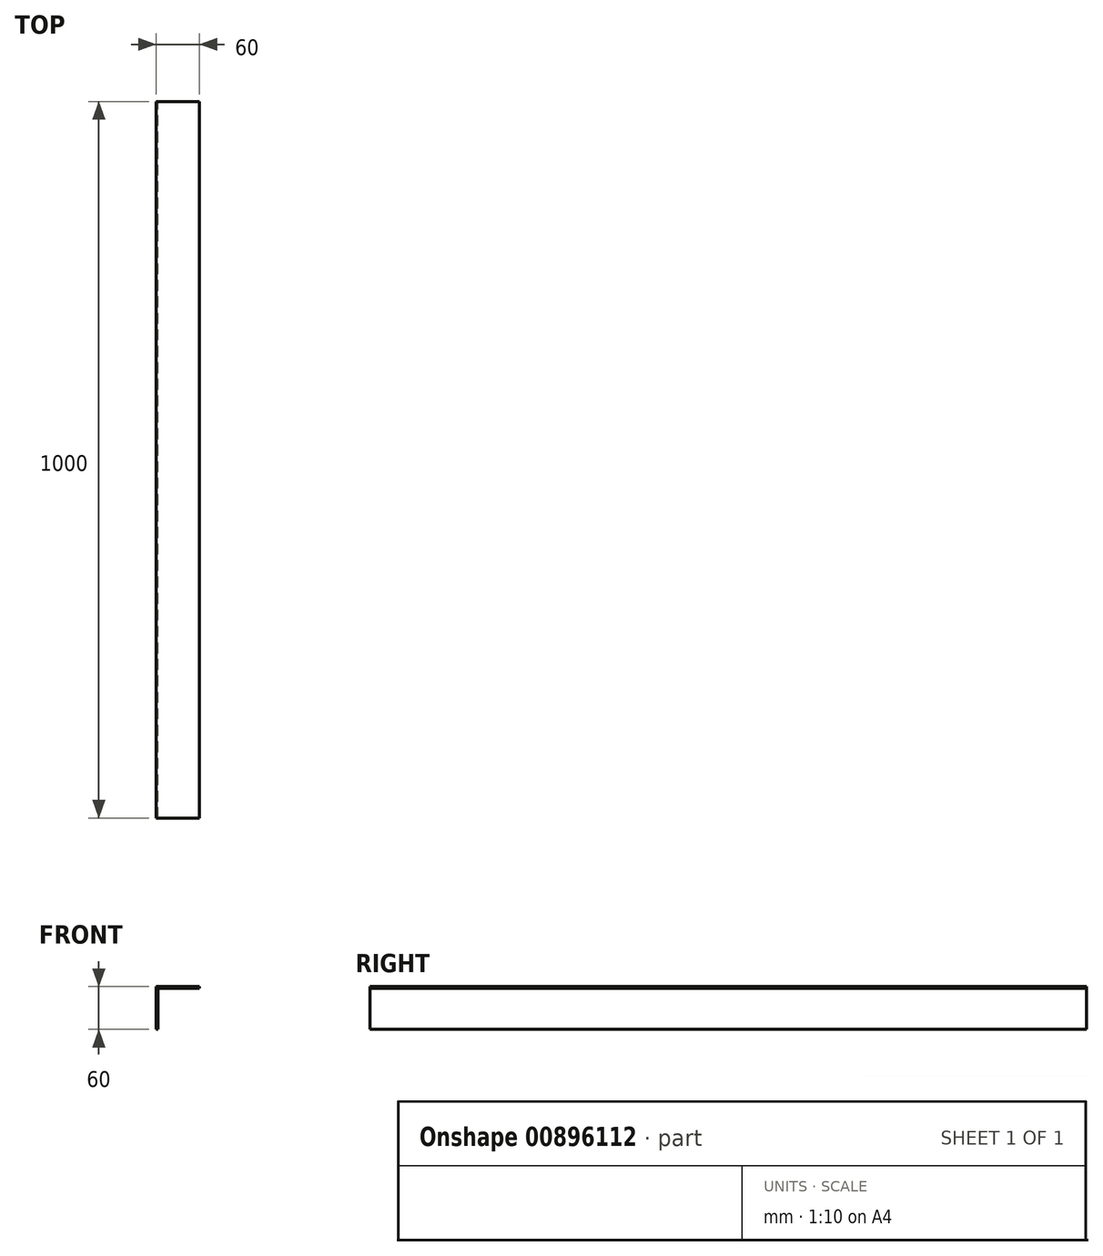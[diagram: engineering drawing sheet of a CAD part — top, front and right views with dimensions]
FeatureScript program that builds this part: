
annotation { "Feature Type Name" : "Feature", "Feature Type Description" : "" }
export const myFeature = defineFeature(function(context is Context, id is Id, definition is map)
    precondition{}
    {
        {
            var Q0;
            Q0=qCreatedBy(makeId("Front.planeOp"),FACE);
            var sketch = newSketch(context, id + "F0", { "sketchPlane" : qUnion([Q0])});
            skLineSegment(sketch, "E0", {"start": v(0, 0) * mm, "end": v(60, 0) * mm});
            skLineSegment(sketch, "E1", {"start": v(60, 0) * mm, "end": v(60, -2.5) * mm});
            skLineSegment(sketch, "E2", {"start": v(60, -2.5) * mm, "end": v(2.5, -2.5) * mm});
            skLineSegment(sketch, "E3", {"start": v(2.5, -2.5) * mm, "end": v(2.5, -60) * mm});
            skLineSegment(sketch, "E4", {"start": v(2.5, -60) * mm, "end": v(0, -60) * mm});
            skLineSegment(sketch, "E5", {"start": v(0, -60) * mm, "end": v(0, 0) * mm});
            skSolve(sketch);
        }
        {
            var Q0;
            Q0 = qSketchRegion(id + "F0", true);
            extrude(context, id + "F1", {"entities" : qUnion([Q0]), "depth" : 1000 * mm, "offsetDistance" : 25 * mm});
        }
    });
